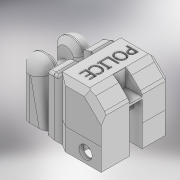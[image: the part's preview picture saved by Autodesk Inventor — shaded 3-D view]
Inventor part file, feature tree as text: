
AUTODESK INVENTOR PART (.ipt)
format: ipt  version: 2022 (Build 260153000, 153)  size: 611,840 bytes
history: native  units: mm
features: sketch x16, extrude x13, fillet x6, chamfer x5, projected_geometry x3, plane x1
ambient origin geometry x8: Origin, YZ Plane, XZ Plane, XY Plane, X Axis, Y Axis, Z Axis, Center Point
bodies: Solid1 (feature_tree)
feature tree (44):
  extrude  "Extrusion1"  Depth=26.5mm TaperAngle=0.0deg
  sketch  "Sketch2"  dims[d4=8.6mm d5=8.0mm d6=0.0mm]
  extrude  "Extrusion2"  Depth=8.0mm TaperAngle=0.0deg
  extrude  "Extrusion3"  Depth=3.1mm
  extrude  "Extrusion4"  Depth=9.5mm TaperAngle=0.0deg
  extrude  "Extrusion5"  Depth=52.281mm TaperAngle=0.0deg
  sketch  "Sketch5"  dims[d12=8.469mm d13=0.0mm d14=52.281mm d15=0.0mm]
  extrude  "Extrusion6"  Depth=2.0mm
  extrude  "Extrusion7"  Depth=8.9mm
  fillet  "Fillet1"  Radius=4.0mm
  extrude  "Extrusion8"  Depth=1.5mm
  sketch  "Sketch10"  dims[d26=15.0mm d27=0.0mm d28=5.0mm]
  extrude  "Extrusion9"  Depth=5.0mm
  sketch  "Sketch11"  dims[d29=15.0mm d30=0.0mm d31=11.75mm d32=0.0mm]
  extrude  "Extrusion10"  Depth=11.75mm TaperAngle=0.0deg
  extrude  "Extrusion11"  Depth=5.0mm
  chamfer  "Chamfer1"  Distance=11.75mm
  fillet  "Fillet2"  Radius=5.0mm
  chamfer  "Chamfer3"  Distance=2.0mm Angle=45.0deg
  chamfer  "Chamfer4"  Distance=2.0mm Angle=45.0deg
  fillet  "Fillet6"  Radius=1.0mm
  fillet  "Fillet7"  Radius=5.0mm
  chamfer  "Chamfer6"  Distance=2.0mm Angle=45.0deg
  chamfer  "Chamfer7"  Distance=2.0mm Angle=45.0deg
  fillet  "Fillet9"  Radius=1.0mm
  fillet  "Fillet10"  Radius=1.0mm
  sketch  "Sketch14"  dims[d68=6.25mm d69=0.0mm d70=1.0mm d71=0.0mm]
  sketch  "Sketch15"
  extrude  "Extrusion12"  Depth=1.0mm TaperAngle=0.0deg
  extrude  "Extrusion13"  [1 undecoded]
  plane  "Work Plane2"
  sketch  "Sketch1"  dims[d0=26.5mm d1=0.0mm d2=26.5mm d3=0.0mm]
  projected_geometry  "Projected Loop1"
  sketch  "Sketch3"  dims[d7=4.9mm d8=3.1mm]
  sketch  "Sketch4"  dims[d9=3.95mm d10=9.5mm d11=0.0mm]
  projected_geometry  "Projected Loop2"
  sketch  "Sketch6"  dims[d16=5.25mm d17=0.0mm d18=2.0mm]
  projected_geometry  "Projected Loop3"
  sketch  "Sketch8"  dims[d19=4.235mm d20=0.0mm d21=8.9mm d22=4.0mm]
  sketch  "Sketch9"  dims[d24=1.5mm d25=1.5mm]
  sketch  "Sketch12"  dims[d34=20.216436mm d35=5.0mm d36=11.75mm d37=0.0mm]
  sketch  "Sketch13"  dims[d38=2.0mm d39=2.0mm d40=45.0deg d44=5.0mm d45=2.0mm d46=2.0mm d47=45.0deg d48=2.0mm d49=2.0mm d50=45.0deg d54=1.0mm d55=5.0mm d60=2.0mm d61=2.0mm d62=45.0deg d63=2.0mm d64=2.0mm d65=45.0deg d66=1.0mm d67=1.0mm]
  sketch  "Sketch16"
  sketch  "Sketch17"
note: 1 required parameter value undecoded (feature->parameter linkage not recoverable at this tier; creation-order binding heuristic only, values carry confidence <= 0.55)
